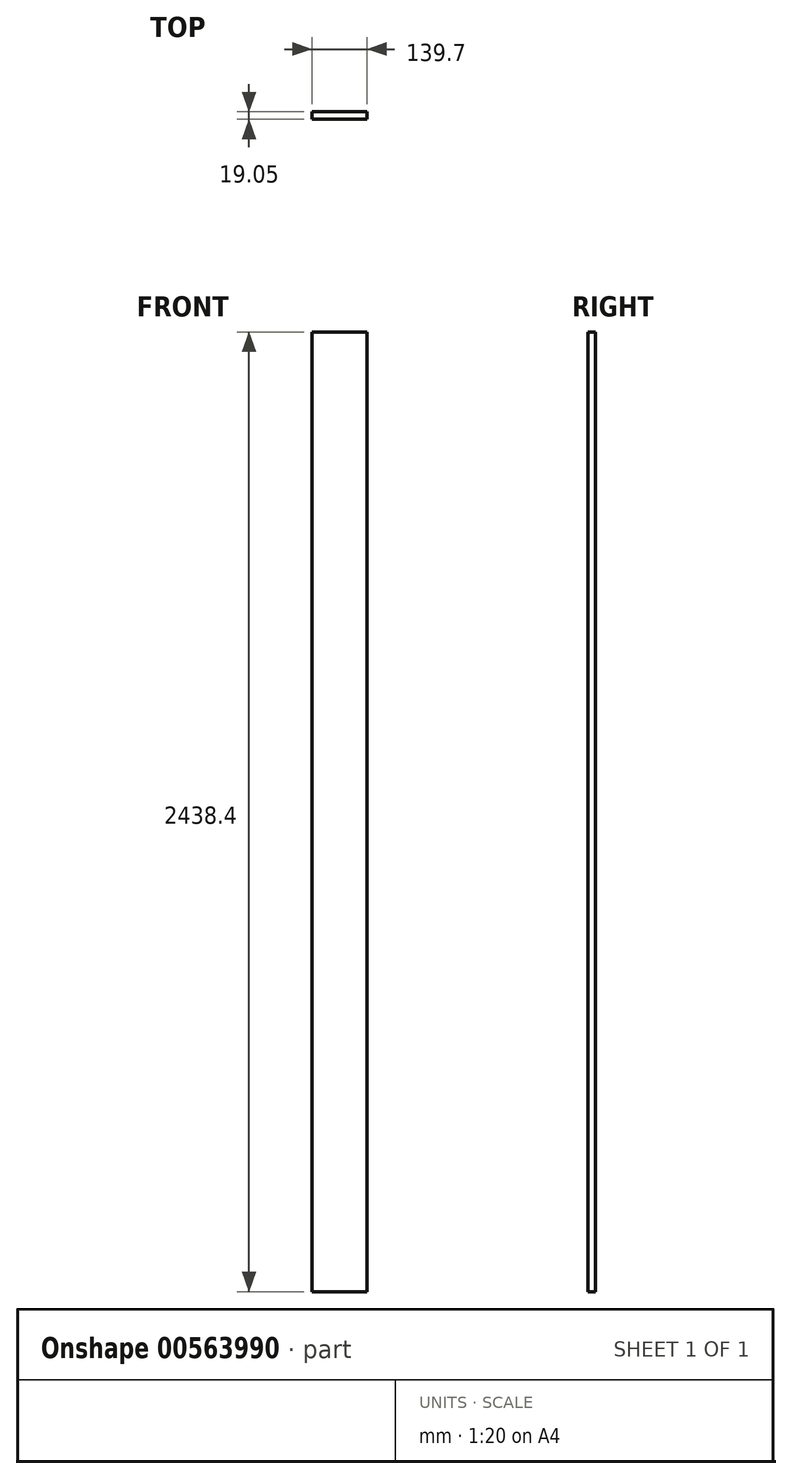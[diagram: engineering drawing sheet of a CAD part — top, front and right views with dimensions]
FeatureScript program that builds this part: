
annotation { "Feature Type Name" : "Feature", "Feature Type Description" : "" }
export const myFeature = defineFeature(function(context is Context, id is Id, definition is map)
    precondition{}
    {
        {
            var Q0;
            Q0=qCreatedBy(makeId("Top.planeOp"),FACE);
            var sketch = newSketch(context, id + "F0", { "sketchPlane" : qUnion([Q0])});
            skLineSegment(sketch, "E0.bottom", {"start": v(0, 0) * mm, "end": v(139.7, 0) * mm});
            skLineSegment(sketch, "E0.top", {"start": v(0, 19.05) * mm, "end": v(139.7, 19.05) * mm});
            skLineSegment(sketch, "E0.left", {"start": v(0, 0) * mm, "end": v(0, 19.05) * mm});
            skLineSegment(sketch, "E0.right", {"start": v(139.7, 0) * mm, "end": v(139.7, 19.05) * mm});
            skSolve(sketch);
        }
        {
            var Q0;
            Q0=qSketchRegion(id+"F0",true);
            extrude(context, id + "F1", {"entities" : qUnion([Q0]), "depth" : 2438.4 * mm});
        }
    });
